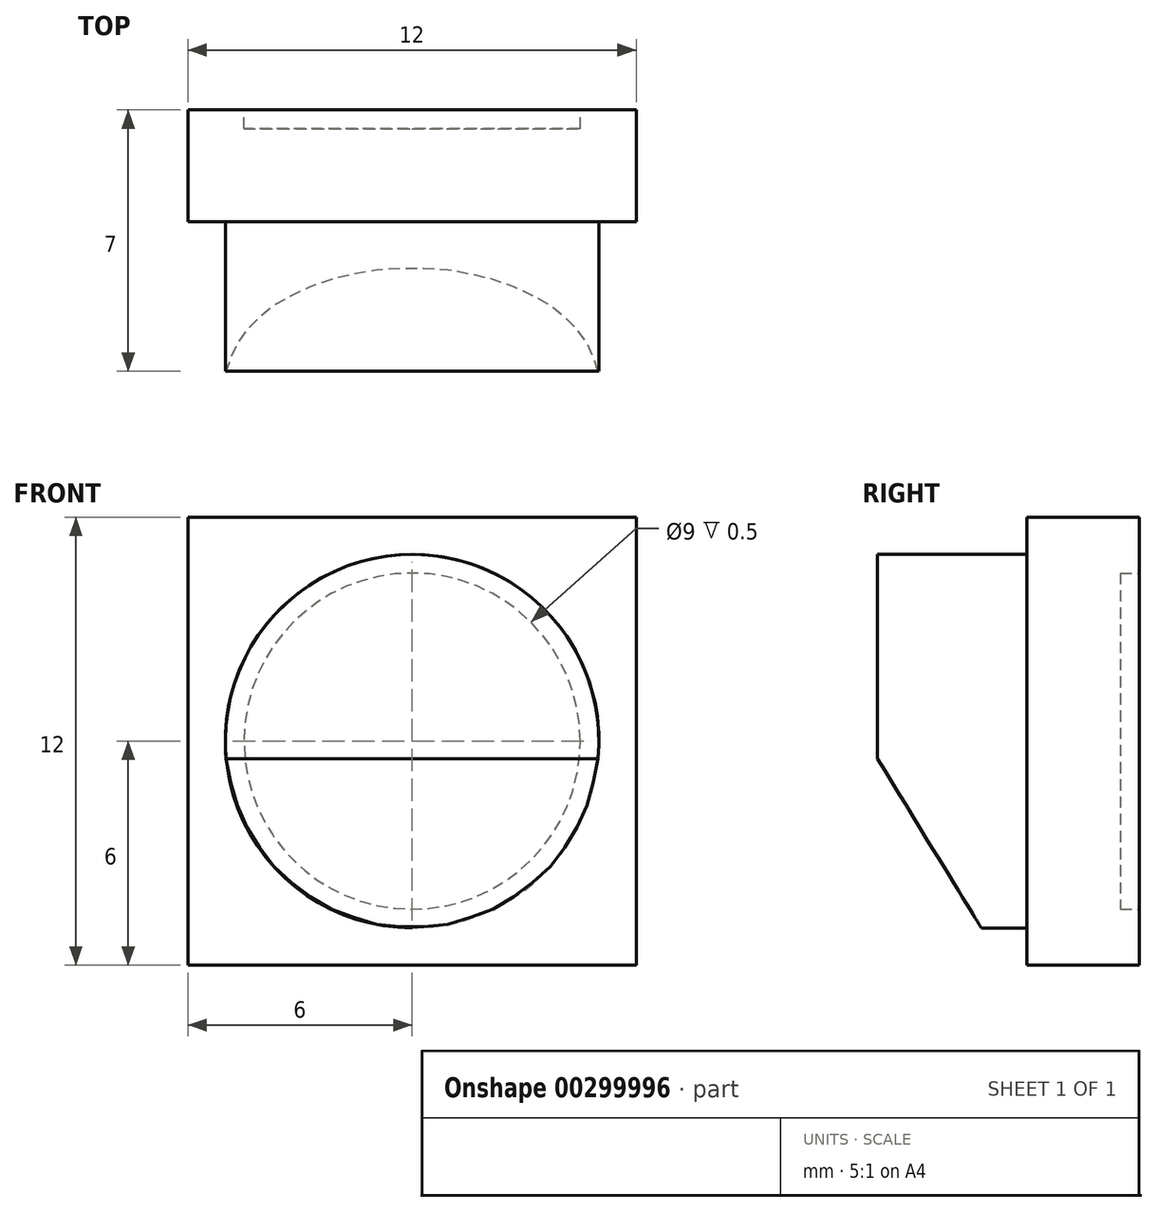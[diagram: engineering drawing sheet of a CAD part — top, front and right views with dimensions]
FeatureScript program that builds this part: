
annotation { "Feature Type Name" : "Feature", "Feature Type Description" : "" }
export const myFeature = defineFeature(function(context is Context, id is Id, definition is map)
    precondition{}
    {
        {
            var Q0;
            Q0=qCreatedBy(makeId("Front.planeOp"),FACE);
            var sketch = newSketch(context, id + "F0", { "sketchPlane" : qUnion([Q0])});
            skCircle(sketch, "E0", {"center": v(0, 0) * mm, "radius": 5 * mm});
            skSolve(sketch);
        }
        {
            var Q0;
            Q0=makeQuery(id+"F0.imprint","IMPRINT",FACE,{"disambiguationData":[TD([[makeQuery(id+"F0.imprint","IMPRINT",EDGE,{"derivedFrom":sQuery(id+"F0.wireOp",EDGE,"E0")}),1.0]])]});
            extrude(context, id + "F1", {"entities" : qUnion([Q0]), "depth" : 4 * mm});
        }
        {
            var Q0;
            Q0=qCreatedBy(makeId("Right.planeOp"),FACE);
            var sketch = newSketch(context, id + "F2", { "sketchPlane" : qUnion([Q0])});
            skLineSegment(sketch, "E1", {"start": v(-0.72, -5.83) * mm, "end": v(-4.3, 0) * mm});
            skLineSegment(sketch, "E2", {"start": v(-4.3, 0) * mm, "end": v(-5.13, -6.03) * mm});
            skLineSegment(sketch, "E3", {"start": v(-5.13, -6.03) * mm, "end": v(-0.72, -5.83) * mm});
            skSolve(sketch);
        }
        {
            var Q0;
            Q0 = qSketchRegion(id + "F2", true);
            extrude(context, id + "F3", {"entities" : qUnion([Q0]), "operationType" : NewBodyOperationType.REMOVE, "endBound" : BoundingType.SYMMETRIC, "oppositeDirection" : true, "depth" : 25 * mm});
        }
        {
            var Q0;
            Q0=makeQuery(id+"F1.opExtrude","CAP_FACE",FACE,{"disambiguationData":[OSD([sQuery(id+"F0.wireOp",EDGE,"E0")])],"isStart":true});
            var sketch = newSketch(context, id + "F4", { "sketchPlane" : qUnion([Q0])});
            skLineSegment(sketch, "E4.bottom", {"start": v(-6, -6) * mm, "end": v(6, -6) * mm});
            skLineSegment(sketch, "E4.top", {"start": v(-6, 6) * mm, "end": v(6, 6) * mm});
            skLineSegment(sketch, "E4.left", {"start": v(-6, -6) * mm, "end": v(-6, 6) * mm});
            skLineSegment(sketch, "E4.right", {"start": v(6, -6) * mm, "end": v(6, 6) * mm});
            skPoint(sketch, "E4.middle", {"position": v(0, 0) * mm});
            skSolve(sketch);
        }
        {
            var Q0;
            Q0 = qSketchRegion(id + "F4", true);
            extrude(context, id + "F5", {"entities" : qUnion([Q0]), "operationType" : NewBodyOperationType.ADD, "depth" : 3 * mm});
        }
        {
            var Q0;
            Q0=makeQuery(id+"F5.opExtrude","CAP_FACE",FACE,{"disambiguationData":[OSD([sQuery(id+"F4.wireOp",EDGE,"E4.bottom"),sQuery(id+"F4.wireOp",EDGE,"E4.top"),sQuery(id+"F4.wireOp",EDGE,"E4.left"),sQuery(id+"F4.wireOp",EDGE,"E4.right")])],"isStart":false});
            var sketch = newSketch(context, id + "F6", { "sketchPlane" : qUnion([Q0])});
            skCircle(sketch, "E5", {"center": v(0, 0) * mm, "radius": 4.5 * mm});
            skSolve(sketch);
        }
        {
            var Q0;
            Q0=makeQuery(id+"F6.imprint","IMPRINT",FACE,{"disambiguationData":[TD([[makeQuery(id+"F6.imprint","IMPRINT",EDGE,{"derivedFrom":sQuery(id+"F6.wireOp",EDGE,"E5")}),1.0]])]});
            extrude(context, id + "F7", {"entities" : qUnion([Q0]), "operationType" : NewBodyOperationType.REMOVE, "oppositeDirection" : true, "depth" : .5 * mm});
        }
    });
